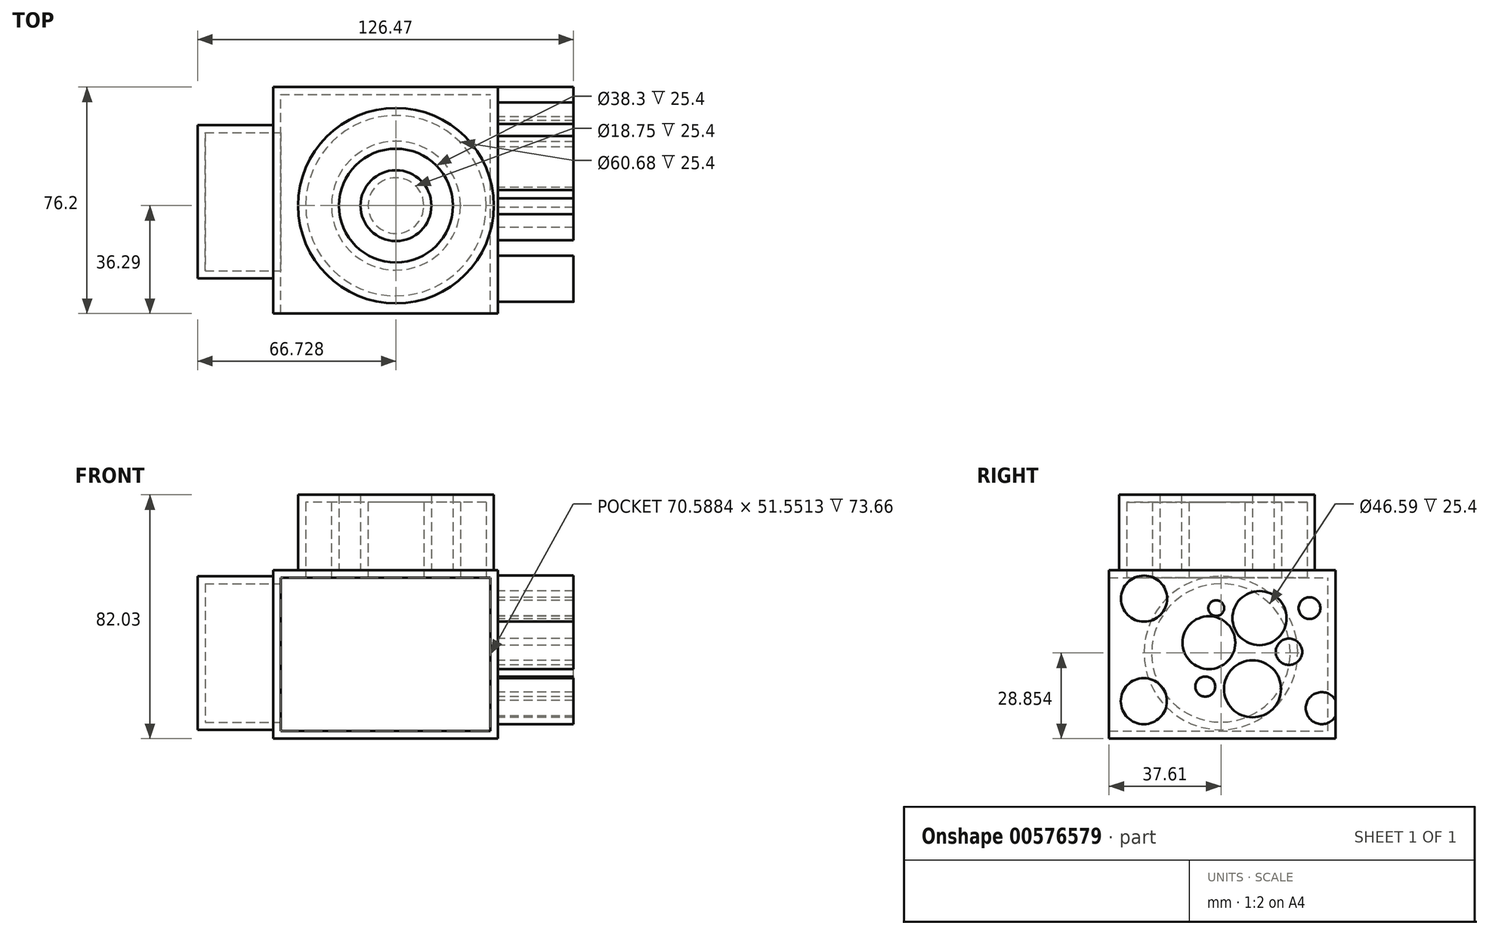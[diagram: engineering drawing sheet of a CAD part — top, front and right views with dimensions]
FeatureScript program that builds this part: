
annotation { "Feature Type Name" : "Feature", "Feature Type Description" : "" }
export const myFeature = defineFeature(function(context is Context, id is Id, definition is map)
    precondition{}
    {
        {
            var Q0;
            Q0=qCreatedBy(makeId("Front.planeOp"),FACE);
            var sketch = newSketch(context, id + "F0", { "sketchPlane" : qUnion([Q0])});
            skLineSegment(sketch, "E0.bottom", {"start": v(0, 0) * mm, "end": v(75.67, 0) * mm});
            skLineSegment(sketch, "E0.top", {"start": v(0, 56.63) * mm, "end": v(75.67, 56.63) * mm});
            skLineSegment(sketch, "E0.left", {"start": v(0, 0) * mm, "end": v(0, 56.63) * mm});
            skLineSegment(sketch, "E0.right", {"start": v(75.67, 0) * mm, "end": v(75.67, 56.63) * mm});
            skSolve(sketch);
        }
        {
            var Q0;
            Q0=makeQuery(id+"F0.imprint","IMPRINT",FACE,{"disambiguationData":[TD([[makeQuery(id+"F0.imprint","IMPRINT",EDGE,{"derivedFrom":sQuery(id+"F0.wireOp",EDGE,"E0.bottom")}),1.0]])]});
            extrude(context, id + "F1", {"entities" : qUnion([Q0]), "depth" : 76.2 * mm, "offsetDistance" : 25.4 * mm});
        }
        {
            var Q0;
            Q0=makeQuery(id+"F1.opExtrude","SWEPT_FACE",FACE,{"disambiguationData":[OSD([sQuery(id+"F0.wireOp",EDGE,"E0.top")])]});
            var sketch = newSketch(context, id + "F2", { "sketchPlane" : qUnion([Q0])});
            skPoint(sketch, "E1", {"position": v(41.33, -39.91) * mm});
            skCircle(sketch, "E2", {"center": v(41.33, -39.91) * mm, "radius": 11.91 * mm});
            skCircle(sketch, "E3", {"center": v(41.33, -39.91) * mm, "radius": 27.34 * mm});
            skCircle(sketch, "E4", {"center": v(41.33, -39.91) * mm, "radius": 32.88 * mm});
            skCircle(sketch, "E5", {"center": v(41.33, -39.91) * mm, "radius": 19.15 * mm});
            skSolve(sketch);
        }
        {
            var Q0;
            Q0=makeQuery(id+"F2.imprint","IMPRINT",FACE,{"disambiguationData":[TD([[makeQuery(id+"F2.imprint","IMPRINT",EDGE,{"derivedFrom":sQuery(id+"F2.wireOp",EDGE,"E2")}),1.0]])]});
            var Q1;
            Q1=makeQuery(id+"F2.imprint","IMPRINT",FACE,{"disambiguationData":[TD([[makeQuery(id+"F2.imprint","IMPRINT",EDGE,{"derivedFrom":sQuery(id+"F2.wireOp",EDGE,"E3")}),1.0]])]});
            var Q2;
            Q2=makeQuery(id+"F2.imprint","IMPRINT",FACE,{"disambiguationData":[TD([[makeQuery(id+"F2.imprint","IMPRINT",EDGE,{"derivedFrom":sQuery(id+"F2.wireOp",EDGE,"E3")}),-1.0]])]});
            extrude(context, id + "F3", {"entities" : qUnion([Q0, Q1, Q2]), "operationType" : NewBodyOperationType.ADD, "depth" : 25.4 * mm, "offsetDistance" : 25.4 * mm});
        }
        {
            var Q0;
            Q0=makeQuery(id+"F1.opExtrude","SWEPT_FACE",FACE,{"disambiguationData":[OSD([sQuery(id+"F0.wireOp",EDGE,"E0.left")])]});
            var sketch = newSketch(context, id + "F4", { "sketchPlane" : qUnion([Q0])});
            skPoint(sketch, "E6", {"position": v(38.59, 28.85) * mm});
            skPoint(sketch, "E7", {"position": v(92.97, 52.74) * mm});
            skCircle(sketch, "E8", {"center": v(38.59, 28.85) * mm, "radius": 9.05 * mm});
            skCircle(sketch, "E9", {"center": v(38.59, 28.85) * mm, "radius": 16.78 * mm});
            skCircle(sketch, "E10", {"center": v(38.59, 28.85) * mm, "radius": 25.84 * mm});
            skCircle(sketch, "E11", {"center": v(92.97, 52.74) * mm, "radius": 7.29 * mm});
            skCircle(sketch, "E12", {"center": v(92.97, 52.74) * mm, "radius": 15.84 * mm});
            skSolve(sketch);
        }
        {
            var Q0;
            Q0=makeQuery(id+"F4.imprint","IMPRINT",FACE,{"disambiguationData":[TD([[makeQuery(id+"F4.imprint","IMPRINT",EDGE,{"derivedFrom":sQuery(id+"F4.wireOp",EDGE,"E9")}),-1.0]])]});
            var Q1;
            Q1=makeQuery(id+"F4.imprint","IMPRINT",FACE,{"disambiguationData":[TD([[makeQuery(id+"F4.imprint","IMPRINT",EDGE,{"derivedFrom":sQuery(id+"F4.wireOp",EDGE,"E8")}),-1.0]])]});
            var Q2;
            Q2=makeQuery(id+"F4.imprint","IMPRINT",FACE,{"disambiguationData":[TD([[makeQuery(id+"F4.imprint","IMPRINT",EDGE,{"derivedFrom":sQuery(id+"F4.wireOp",EDGE,"E8")}),1.0]])]});
            extrude(context, id + "F5", {"entities" : qUnion([Q0, Q1, Q2]), "operationType" : NewBodyOperationType.ADD, "depth" : 25.4 * mm, "offsetDistance" : 25.4 * mm});
        }
        {
            var Q0;
            Q0=makeQuery(id+"F1.opExtrude","CAP_FACE",FACE,{"disambiguationData":[OSD([sQuery(id+"F0.wireOp",EDGE,"E0.bottom"),sQuery(id+"F0.wireOp",EDGE,"E0.top"),sQuery(id+"F0.wireOp",EDGE,"E0.left"),sQuery(id+"F0.wireOp",EDGE,"E0.right")])],"isStart":false});
            shell(context, id + "F6", {"entities" : qUnion([Q0]), "thickness" : 2.54 * mm});
        }
        {
            var Q0;
            Q0=makeQuery(id+"F1.opExtrude","SWEPT_FACE",FACE,{"disambiguationData":[OSD([sQuery(id+"F0.wireOp",EDGE,"E0.right")])]});
            var sketch = newSketch(context, id + "F7", { "sketchPlane" : qUnion([Q0])});
            skPoint(sketch, "E13", {"position": v(-32.53, 29.23) * mm});
            skCircle(sketch, "E14", {"center": v(-32.53, 29.23) * mm, "radius": 23.14 * mm});
            skCircle(sketch, "E15", {"center": v(-27.96, 16.77) * mm, "radius": 9.6 * mm});
            skCircle(sketch, "E16", {"center": v(-42.62, 32.3) * mm, "radius": 8.88 * mm});
            skCircle(sketch, "E17", {"center": v(-25.61, 40.55) * mm, "radius": 9.1 * mm});
            skCircle(sketch, "E18", {"center": v(-15.7, 29.23) * mm, "radius": 4.44 * mm});
            skCircle(sketch, "E19", {"center": v(-43.85, 17.55) * mm, "radius": 3.37 * mm});
            skCircle(sketch, "E20", {"center": v(-40.16, 43.93) * mm, "radius": 2.65 * mm});
            skCircle(sketch, "E21", {"center": v(-64.52, 12.63) * mm, "radius": 7.74 * mm});
            skCircle(sketch, "E22", {"center": v(-64.44, 47.11) * mm, "radius": 7.74 * mm});
            skCircle(sketch, "E23", {"center": v(-4.68, 10.28) * mm, "radius": 5.37 * mm});
            skCircle(sketch, "E24", {"center": v(-8.8, 43.93) * mm, "radius": 3.66 * mm});
            skSolve(sketch);
        }
        {
            var Q0;
            Q0=makeQuery(id+"F7.imprint","IMPRINT",FACE,{"disambiguationData":[TD([[makeQuery(id+"F7.imprint","IMPRINT",EDGE,{"derivedFrom":sQuery(id+"F7.wireOp",EDGE,"E24")}),1.0]])]});
            var Q1;
            Q1=makeQuery(id+"F7.imprint","IMPRINT",FACE,{"disambiguationData":[TD([[makeQuery(id+"F7.imprint","IMPRINT",EDGE,{"derivedFrom":sQuery(id+"F7.wireOp",EDGE,"E17")}),1.0]])]});
            var Q2;
            Q2=makeQuery(id+"F7.imprint","IMPRINT",FACE,{"disambiguationData":[TD([[makeQuery(id+"F7.imprint","IMPRINT",EDGE,{"derivedFrom":sQuery(id+"F7.wireOp",EDGE,"E20")}),1.0]])]});
            var Q3;
            Q3=makeQuery(id+"F7.imprint","IMPRINT",FACE,{"disambiguationData":[TD([[makeQuery(id+"F7.imprint","IMPRINT",EDGE,{"derivedFrom":sQuery(id+"F7.wireOp",EDGE,"E16")}),1.0]])]});
            var Q4;
            Q4=makeQuery(id+"F7.imprint","IMPRINT",FACE,{"disambiguationData":[TD([[makeQuery(id+"F7.imprint","IMPRINT",EDGE,{"derivedFrom":sQuery(id+"F7.wireOp",EDGE,"E19")}),1.0]])]});
            var Q5;
            Q5=makeQuery(id+"F7.imprint","IMPRINT",FACE,{"disambiguationData":[TD([[makeQuery(id+"F7.imprint","IMPRINT",EDGE,{"derivedFrom":sQuery(id+"F7.wireOp",EDGE,"E15")}),1.0]])]});
            var Q6;
            Q6=makeQuery(id+"F7.imprint","IMPRINT",FACE,{"disambiguationData":[TD([[makeQuery(id+"F7.imprint","IMPRINT",EDGE,{"derivedFrom":sQuery(id+"F7.wireOp",EDGE,"E18")}),1.0]])]});
            var Q7;
            {var subQ0=sQuery(id+"F7.wireOp",EDGE,"E23");var subQ1=makeQuery(id+"F1.opExtrude","CAP_EDGE",EDGE,{"disambiguationData":[OSD([sQuery(id+"F0.wireOp",EDGE,"E0.right")])],"isStart":true});var subQ2=makeQuery(id+"F7.imprint","INTERSECT",VERTEX,{"disambiguationData":[OD(0.0)],"derivedFrom":[subQ1,subQ0]});Q7=makeQuery(id+"F7.imprint","IMPRINT",FACE,{"disambiguationData":[TD([[makeQuery(id+"F7.imprint","IMPRINT",EDGE,{"disambiguationData":[TD([[subQ2,1.0]])],"derivedFrom":subQ0}),1.0]])]});}
            var Q8;
            Q8=makeQuery(id+"F7.imprint","IMPRINT",FACE,{"disambiguationData":[TD([[makeQuery(id+"F7.imprint","IMPRINT",EDGE,{"derivedFrom":sQuery(id+"F7.wireOp",EDGE,"E22")}),1.0]])]});
            var Q9;
            Q9=makeQuery(id+"F7.imprint","IMPRINT",FACE,{"disambiguationData":[TD([[makeQuery(id+"F7.imprint","IMPRINT",EDGE,{"derivedFrom":sQuery(id+"F7.wireOp",EDGE,"E21")}),1.0]])]});
            extrude(context, id + "F8", {"entities" : qUnion([Q0, Q1, Q2, Q3, Q4, Q5, Q6, Q7, Q8, Q9]), "operationType" : NewBodyOperationType.ADD, "depth" : 25.4 * mm, "offsetDistance" : 25.4 * mm});
        }
    });
